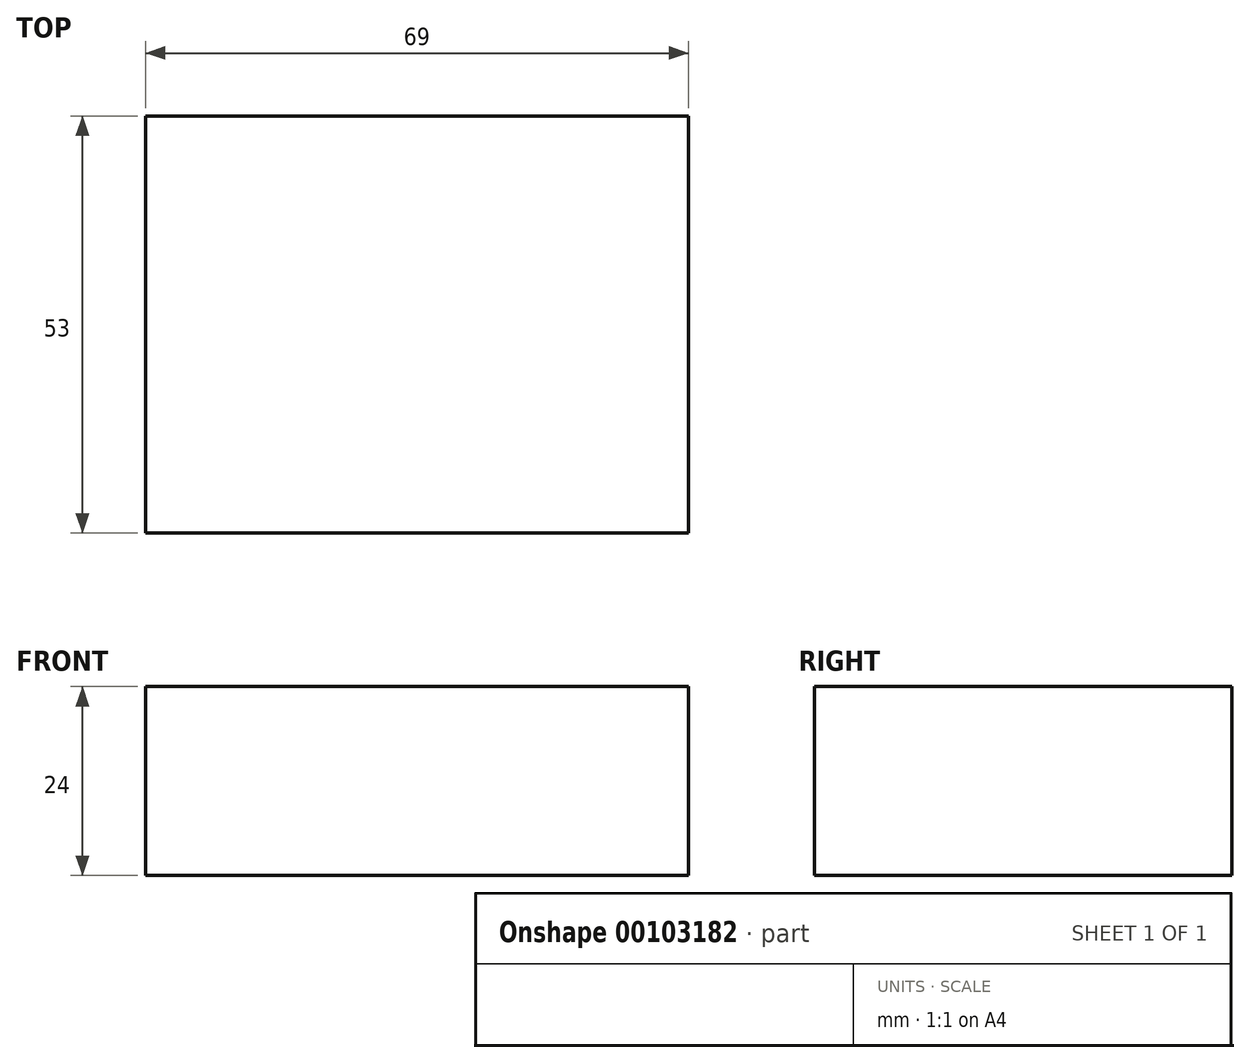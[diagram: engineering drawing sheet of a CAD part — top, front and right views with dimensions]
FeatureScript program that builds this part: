
annotation { "Feature Type Name" : "Feature", "Feature Type Description" : "" }
export const myFeature = defineFeature(function(context is Context, id is Id, definition is map)
    precondition{}
    {
        {
            var Q0;
            Q0=qCreatedBy(makeId("Top.planeOp"),FACE);
            var sketch = newSketch(context, id + "F0", { "sketchPlane" : qUnion([Q0])});
            skLineSegment(sketch, "E0.bottom", {"start": v(34.5, -26.5) * mm, "end": v(-34.5, -26.5) * mm});
            skLineSegment(sketch, "E0.top", {"start": v(34.5, 26.5) * mm, "end": v(-34.5, 26.5) * mm});
            skLineSegment(sketch, "E0.left", {"start": v(34.5, -26.5) * mm, "end": v(34.5, 26.5) * mm});
            skLineSegment(sketch, "E0.right", {"start": v(-34.5, -26.5) * mm, "end": v(-34.5, 26.5) * mm});
            skPoint(sketch, "E0.middle", {"position": v(0, 0) * mm});
            skSolve(sketch);
        }
        {
            var Q0;
            Q0=makeQuery(id+"F0.imprint","IMPRINT",FACE,{"disambiguationData":[TD([[makeQuery(id+"F0.imprint","IMPRINT",EDGE,{"derivedFrom":sQuery(id+"F0.wireOp",EDGE,"E0.bottom")}),-1.0]])]});
            extrude(context, id + "F1", {"entities" : qUnion([Q0]), "depth" : 24 * mm});
        }
    });
